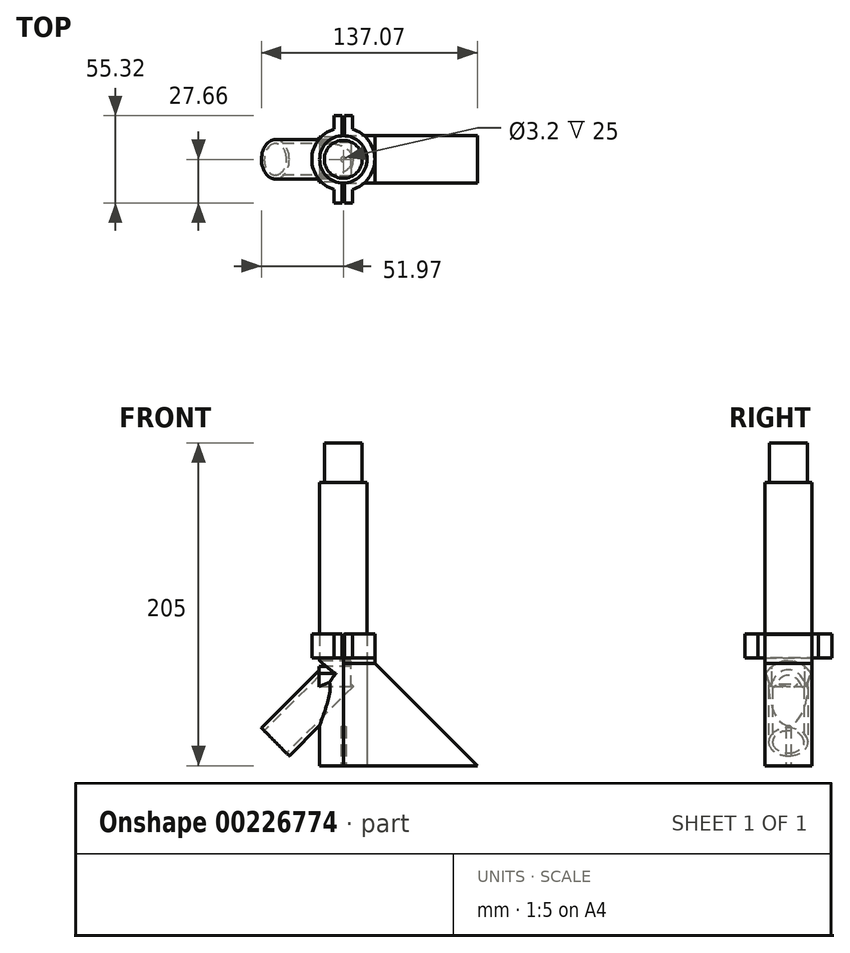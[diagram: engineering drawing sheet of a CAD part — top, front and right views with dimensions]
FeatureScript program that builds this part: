
annotation { "Feature Type Name" : "Feature", "Feature Type Description" : "" }
export const myFeature = defineFeature(function(context is Context, id is Id, definition is map)
    precondition{}
    {
        {
            var Q0;
            Q0=qCreatedBy(makeId("Top.planeOp"),FACE);
            var sketch = newSketch(context, id + "F0", { "sketchPlane" : qUnion([Q0])});
            skCircle(sketch, "E0", {"center": v(0, 0) * mm, "radius": 12 * mm});
            skCircle(sketch, "E1", {"center": v(0, 0) * mm, "radius": 15 * mm});
            skLineSegment(sketch, "E2", {"start": v(0, 15) * mm, "end": v(0, -15) * mm});
            skLineSegment(sketch, "E3", {"start": v(0, -15) * mm, "end": v(-56.85, -15) * mm});
            skLineSegment(sketch, "E4", {"start": v(-56.85, -15) * mm, "end": v(-56.85, 15) * mm});
            skLineSegment(sketch, "E5", {"start": v(-56.85, 15) * mm, "end": v(0, 15) * mm});
            skSolve(sketch);
        }
        {
            var Q0;
            {var subQ3=sQuery(id+"F0.wireOp",EDGE,"E3");Q0=makeQuery(id+"F0.imprint","IMPRINT",FACE,{"disambiguationData":[TD([[makeQuery(id+"F0.imprint","IMPRINT",EDGE,{"derivedFrom":subQ3}),-1.0]])]});}
            extrude(context, id + "F1", {"entities" : qUnion([Q0]), "depth" : 205 * mm});
        }
        {
            var Q0;
            Q0=makeQuery(id+"F0.imprint","IMPRINT",FACE,{"disambiguationData":[TD([[makeQuery(id+"F0.imprint","IMPRINT",EDGE,{"derivedFrom":sQuery(id+"F0.wireOp",EDGE,"E0")}),1.0]])]});
            var Q1;
            Q1=makeQuery(id+"F0.imprint","IMPRINT",FACE,{"disambiguationData":[TD([[makeQuery(id+"F0.imprint","IMPRINT",EDGE,{"derivedFrom":sQuery(id+"F0.wireOp",EDGE,"E0")}),-1.0]])]});
            extrude(context, id + "F2", {"entities" : qUnion([Q0, Q1]), "operationType" : NewBodyOperationType.ADD, "depth" : 10 * mm});
        }
        {
            var Q0;
            {var subQ0=sQuery(id+"F0.wireOp",EDGE,"E1");Q0=makeQuery(id+"F2.boolean.opBoolean","MERGE",FACE,{"derivedFrom":[makeQuery(id+"F1.opExtrude","CAP_FACE",FACE,{"disambiguationData":[OSD([sQuery(id+"F0.wireOp",EDGE,"E0"),subQ0])],"isStart":true}),makeQuery(id+"F2.opExtrude","CAP_FACE",FACE,{"disambiguationData":[OSD([subQ0])],"isStart":true})]});}
            var sketch = newSketch(context, id + "F3", { "sketchPlane" : qUnion([Q0])});
            skLineSegment(sketch, "E6.bottom", {"start": v(-1.5, -1.5) * mm, "end": v(1.5, -1.5) * mm});
            skLineSegment(sketch, "E6.top", {"start": v(-1.5, 1.5) * mm, "end": v(1.5, 1.5) * mm});
            skLineSegment(sketch, "E6.left", {"start": v(-1.5, -1.5) * mm, "end": v(-1.5, 1.5) * mm});
            skLineSegment(sketch, "E6.right", {"start": v(1.5, -1.5) * mm, "end": v(1.5, 1.5) * mm});
            skPoint(sketch, "E6.middle", {"position": v(0, 0) * mm});
            skCircle(sketch, "E7", {"center": v(0, 0) * mm, "radius": 2.12 * mm});
            skSolve(sketch);
        }
        {
            var Q0;
            {var subQ0=sQuery(id+"F3.wireOp",EDGE,"E6.left");Q0=makeQuery(id+"F3.imprint","IMPRINT",FACE,{"disambiguationData":[TD([[makeQuery(id+"F3.imprint","IMPRINT",EDGE,{"derivedFrom":subQ0}),1.0]])]});}
            var Q1;
            {var subQ0=sQuery(id+"F3.wireOp",EDGE,"E6.bottom");Q1=makeQuery(id+"F3.imprint","IMPRINT",FACE,{"disambiguationData":[TD([[makeQuery(id+"F3.imprint","IMPRINT",EDGE,{"derivedFrom":subQ0}),-1.0]])]});}
            var Q2;
            {var subQ0=sQuery(id+"F3.wireOp",EDGE,"E6.top");Q2=makeQuery(id+"F3.imprint","IMPRINT",FACE,{"disambiguationData":[TD([[makeQuery(id+"F3.imprint","IMPRINT",EDGE,{"derivedFrom":subQ0}),1.0]])]});}
            var Q3;
            {var subQ0=sQuery(id+"F3.wireOp",EDGE,"E6.right");Q3=makeQuery(id+"F3.imprint","IMPRINT",FACE,{"disambiguationData":[TD([[makeQuery(id+"F3.imprint","IMPRINT",EDGE,{"derivedFrom":subQ0}),-1.0]])]});}
            var Q4;
            Q4=makeQuery(id+"F3.imprint","IMPRINT",FACE,{"disambiguationData":[TD([[makeQuery(id+"F3.imprint","IMPRINT",EDGE,{"derivedFrom":sQuery(id+"F3.wireOp",EDGE,"E6.bottom")}),1.0]])]});
            extrude(context, id + "F4", {"entities" : qUnion([Q0, Q1, Q2, Q3, Q4]), "operationType" : NewBodyOperationType.REMOVE, "oppositeDirection" : true, "depth" : 18 * mm});
        }
        {
            var Q0;
            Q0=qCreatedBy(makeId("Top.planeOp"),FACE);
            var sketch = newSketch(context, id + "F5", { "sketchPlane" : qUnion([Q0])});
            skCircle(sketch, "E8", {"center": v(0, 0) * mm, "radius": 12 * mm});
            skSolve(sketch);
        }
        {
            var Q0;
            Q0=qCreatedBy(makeId("Top.planeOp"),FACE);
            var Q1;
            Q1=qCreatedBy(makeId("Right.planeOp"),FACE);
            cPlane(context, id + "F6", {"entities" : qUnion([Q0, Q1]), "cplaneType" : CPlaneType.MID_PLANE, "offset" : 25 * mm, "flipAlignment" : true, "width" : 150 * mm, "height" : 150 * mm});
        }
        {
            var Q0;
            Q0=qCreatedBy(id+"F6.planeOp",FACE);
            cPlane(context, id + "F7", {"entities" : qUnion([Q0]), "cplaneType" : CPlaneType.OFFSET, "offset" : 19.82 * mm, "oppositeDirection" : true, "width" : 150 * mm, "height" : 150 * mm});
        }
        {
            var Q0;
            Q0=qCreatedBy(id+"F7.planeOp",FACE);
            var sketch = newSketch(context, id + "F8", { "sketchPlane" : qUnion([Q0])});
            skCircle(sketch, "E9", {"center": v(0, 41.17) * mm, "radius": 10 * mm});
            skLineSegment(sketch, "E10.bottom", {"start": v(-15, 56.17) * mm, "end": v(15, 56.17) * mm});
            skLineSegment(sketch, "E10.top", {"start": v(-15, 26.17) * mm, "end": v(15, 26.17) * mm});
            skLineSegment(sketch, "E10.left", {"start": v(-15, 56.17) * mm, "end": v(-15, 26.17) * mm});
            skLineSegment(sketch, "E10.right", {"start": v(15, 56.17) * mm, "end": v(15, 26.17) * mm});
            skCircle(sketch, "E11", {"center": v(0, 41.17) * mm, "radius": 12.5 * mm});
            skSolve(sketch);
        }
        {
            var Q0;
            Q0=makeQuery(id+"F8.imprint","IMPRINT",FACE,{"disambiguationData":[TD([[makeQuery(id+"F8.imprint","IMPRINT",EDGE,{"derivedFrom":sQuery(id+"F8.wireOp",EDGE,"E9")}),-1.0]])]});
            extrude(context, id + "F9", {"entities" : qUnion([Q0]), "depth" : 59 * mm});
        }
        {
            var Q0;
            Q0=makeQuery(id+"F9.opExtrude","SWEPT_BODY",BODY,{"disambiguationData":[OSD([sQuery(id+"F8.wireOp",EDGE,"E9"),sQuery(id+"F8.wireOp",EDGE,"E11")])]});
            var Q1;
            Q1=makeQuery(id+"F1.opExtrude","SWEPT_BODY",BODY,{"disambiguationData":[OSD([sQuery(id+"F0.wireOp",EDGE,"E0"),sQuery(id+"F0.wireOp",EDGE,"E2"),sQuery(id+"F0.wireOp",EDGE,"E3"),sQuery(id+"F0.wireOp",EDGE,"E4"),sQuery(id+"F0.wireOp",EDGE,"E5")])]});
            booleanBodies(context, id + "F10", {"operationType" : BooleanOperationType.INTERSECTION, "tools" : qUnion([Q0, Q1])});
        }
        {
            var Q0;
            Q0=makeQuery(id+"F5.imprint","IMPRINT",FACE,{"disambiguationData":[TD([[makeQuery(id+"F5.imprint","IMPRINT",EDGE,{"derivedFrom":sQuery(id+"F5.wireOp",EDGE,"E8")}),1.0]])]});
            extrude(context, id + "F11", {"entities" : qUnion([Q0]), "depth" : 205 * mm});
        }
        {
            var Q0;
            Q0=makeQuery(id+"F5.imprint","IMPRINT",FACE,{"disambiguationData":[TD([[makeQuery(id+"F5.imprint","IMPRINT",EDGE,{"derivedFrom":sQuery(id+"F5.wireOp",EDGE,"E8")}),1.0]])]});
            var sketch = newSketch(context, id + "F12", { "sketchPlane" : qUnion([Q0])});
            skCircle(sketch, "E12", {"center": v(0, 0) * mm, "radius": 15 * mm});
            skSolve(sketch);
        }
        {
            var Q0;
            Q0=makeQuery(id+"F12.imprint","IMPRINT",FACE,{"disambiguationData":[TD([[makeQuery(id+"F12.imprint","IMPRINT",EDGE,{"derivedFrom":sQuery(id+"F12.wireOp",EDGE,"E12")}),1.0]])]});
            extrude(context, id + "F13", {"entities" : qUnion([Q0]), "depth" : 180 * mm});
        }
        {
            var Q0;
            Q0=makeQuery(id+"F13.opExtrude","CAP_FACE",FACE,{"disambiguationData":[OSD([sQuery(id+"F5.wireOp",EDGE,"E8"),sQuery(id+"F12.wireOp",EDGE,"E12")])],"isStart":true});
            var sketch = newSketch(context, id + "F14", { "sketchPlane" : qUnion([Q0])});
            skCircle(sketch, "E13", {"center": v(0, 0) * mm, "radius": 1.6 * mm});
            skSolve(sketch);
        }
        {
            var Q0;
            Q0=makeQuery(id+"F5.imprint","IMPRINT",FACE,{"disambiguationData":[TD([[makeQuery(id+"F5.imprint","IMPRINT",EDGE,{"derivedFrom":sQuery(id+"F5.wireOp",EDGE,"E8")}),1.0]])]});
            extrude(context, id + "F15", {"entities" : qUnion([Q0]), "operationType" : NewBodyOperationType.ADD, "depth" : 20 * mm});
        }
        {
            var Q0;
            Q0=makeQuery(id+"F14.imprint","IMPRINT",FACE,{"disambiguationData":[TD([[makeQuery(id+"F14.imprint","IMPRINT",EDGE,{"derivedFrom":sQuery(id+"F14.wireOp",EDGE,"E13")}),1.0]])]});
            extrude(context, id + "F16", {"entities" : qUnion([Q0]), "operationType" : NewBodyOperationType.REMOVE, "oppositeDirection" : true, "depth" : 25 * mm});
        }
        {
            var Q0;
            Q0=makeQuery(id+"F8.imprint","IMPRINT",FACE,{"disambiguationData":[TD([[makeQuery(id+"F8.imprint","IMPRINT",EDGE,{"derivedFrom":sQuery(id+"F8.wireOp",EDGE,"E9")}),1.0]])]});
            extrude(context, id + "F17", {"entities" : qUnion([Q0]), "operationType" : NewBodyOperationType.REMOVE, "depth" : 60 * mm});
        }
        {
            var Q0;
            Q0=qCreatedBy(id+"F7.planeOp",FACE);
            cPlane(context, id + "F18", {"entities" : qUnion([Q0]), "cplaneType" : CPlaneType.OFFSET, "offset" : 80 * mm, "width" : 150 * mm, "height" : 150 * mm});
        }
        {
            var Q0;
            {var subQ0=sQuery(id+"F5.wireOp",EDGE,"E8");Q0=makeQuery(id+"F15.boolean.opBoolean","MERGE",FACE,{"derivedFrom":[makeQuery(id+"F13.opExtrude","CAP_FACE",FACE,{"disambiguationData":[OSD([subQ0,sQuery(id+"F12.wireOp",EDGE,"E12")])],"isStart":true}),makeQuery(id+"F15.opExtrude","CAP_FACE",FACE,{"disambiguationData":[OSD([subQ0])],"isStart":true})]});}
            var sketch = newSketch(context, id + "F19", { "sketchPlane" : qUnion([Q0])});
            skLineSegment(sketch, "E14.bottom", {"start": v(-15, -15) * mm, "end": v(85.1, -15) * mm});
            skLineSegment(sketch, "E14.top", {"start": v(-15, 15) * mm, "end": v(85.1, 15) * mm});
            skLineSegment(sketch, "E14.left", {"start": v(-15, -15) * mm, "end": v(-15, 15) * mm});
            skLineSegment(sketch, "E14.right", {"start": v(85.1, -15) * mm, "end": v(85.1, 15) * mm});
            skSolve(sketch);
        }
        {
            var Q0;
            {var subQ0=sQuery(id+"F19.wireOp",EDGE,"E14.right");Q0=makeQuery(id+"F19.imprint","IMPRINT",FACE,{"disambiguationData":[TD([[makeQuery(id+"F19.imprint","IMPRINT",EDGE,{"derivedFrom":subQ0}),1.0]])]});}
            extrude(context, id + "F20", {"entities" : qUnion([Q0]), "oppositeDirection" : true, "depth" : 65 * mm});
        }
        {
            var Q0;
            Q0=qCreatedBy(makeId("Right.planeOp"),FACE);
            cPlane(context, id + "F21", {"entities" : qUnion([Q0]), "cplaneType" : CPlaneType.OFFSET, "offset" : 15 * mm, "oppositeDirection" : true, "width" : 150 * mm, "height" : 150 * mm});
        }
        {
            var Q0;
            Q0=qCreatedBy(id+"F21.planeOp",FACE);
            var sketch = newSketch(context, id + "F22", { "sketchPlane" : qUnion([Q0])});
            skCircle(sketch, "E15", {"center": v(0, 50) * mm, "radius": 18.58 * mm});
            skCircle(sketch, "E16", {"center": v(0, 50) * mm, "radius": 16.65 * mm});
            skLineSegment(sketch, "E17", {"start": v(18.58, 50) * mm, "end": v(-18.58, 50) * mm});
            skLineSegment(sketch, "E18", {"start": v(-10.5, 50) * mm, "end": v(-10.5, 37.08) * mm});
            skLineSegment(sketch, "E19", {"start": v(0, 0) * mm, "end": v(0, 91.56) * mm, "construction": true});
            skLineSegment(sketch, "E20", {"start": v(-11.29, 50) * mm, "end": v(-14.29, 41.45) * mm});
            skLineSegment(sketch, "E21.MirrorCS", {"start": v(10.5, 50) * mm, "end": v(10.5, 37.08) * mm});
            skLineSegment(sketch, "E22.MirrorCS", {"start": v(11.29, 50) * mm, "end": v(14.29, 41.45) * mm});
            skLineSegment(sketch, "E23.MirrorCS", {"start": v(-10.5, 50) * mm, "end": v(-10.5, 62.92) * mm});
            skLineSegment(sketch, "E24.MirrorCS", {"start": v(-11.29, 50) * mm, "end": v(-14.29, 58.55) * mm});
            skLineSegment(sketch, "E25.MirrorCS", {"start": v(10.5, 50) * mm, "end": v(10.5, 62.92) * mm});
            skLineSegment(sketch, "E26.MirrorCS", {"start": v(11.29, 50) * mm, "end": v(14.29, 58.55) * mm});
            skPoint(sketch, "E27", {"position": v(0, 68.58) * mm});
            skSolve(sketch);
        }
        {
            var Q0;
            {var subQ0=sQuery(id+"F22.wireOp",EDGE,"E23.MirrorCS");Q0=makeQuery(id+"F22.imprint","IMPRINT",FACE,{"disambiguationData":[TD([[makeQuery(id+"F22.imprint","IMPRINT",EDGE,{"derivedFrom":subQ0}),-1.0]])]});}
            extrude(context, id + "F23", {"entities" : qUnion([Q0]), "operationType" : NewBodyOperationType.REMOVE, "depth" : 20 * mm});
        }
        {
            var Q0;
            {var subQ0=sQuery(id+"F22.wireOp",EDGE,"E23.MirrorCS");Q0=makeQuery(id+"F22.imprint","IMPRINT",FACE,{"disambiguationData":[TD([[makeQuery(id+"F22.imprint","IMPRINT",EDGE,{"derivedFrom":subQ0}),1.0]])]});}
            var Q1;
            {var subQ0=sQuery(id+"F22.wireOp",EDGE,"E25.MirrorCS");Q1=makeQuery(id+"F22.imprint","IMPRINT",FACE,{"disambiguationData":[TD([[makeQuery(id+"F22.imprint","IMPRINT",EDGE,{"derivedFrom":subQ0}),-1.0]])]});}
            extrude(context, id + "F24", {"entities" : qUnion([Q0, Q1]), "operationType" : NewBodyOperationType.ADD, "depth" : 18 * mm});
        }
        {
            var Q0;
            {var subQ0=sQuery(id+"F22.wireOp",EDGE,"E23.MirrorCS");Q0=makeQuery(id+"F22.imprint","IMPRINT",FACE,{"disambiguationData":[TD([[makeQuery(id+"F22.imprint","IMPRINT",EDGE,{"derivedFrom":subQ0}),1.0]])]});}
            var Q1;
            {var subQ0=sQuery(id+"F22.wireOp",EDGE,"E25.MirrorCS");Q1=makeQuery(id+"F22.imprint","IMPRINT",FACE,{"disambiguationData":[TD([[makeQuery(id+"F22.imprint","IMPRINT",EDGE,{"derivedFrom":subQ0}),-1.0]])]});}
            extrude(context, id + "F25", {"entities" : qUnion([Q0, Q1]), "operationType" : NewBodyOperationType.ADD, "oppositeDirection" : true, "depth" : .5 * mm});
        }
        {
            var Q0;
            Q0=qCreatedBy(makeId("Top.planeOp"),FACE);
            cPlane(context, id + "F26", {"entities" : qUnion([Q0]), "cplaneType" : CPlaneType.OFFSET, "offset" : 68.58 * mm, "width" : 150 * mm, "height" : 150 * mm});
        }
        {
            var Q0;
            Q0=qCreatedBy(id+"F26.planeOp",FACE);
            var sketch = newSketch(context, id + "F27", { "sketchPlane" : qUnion([Q0])});
            skCircle(sketch, "E28", {"center": v(0, 0) * mm, "radius": 15 * mm});
            skCircle(sketch, "E29", {"center": v(0, 0) * mm, "radius": 20 * mm});
            skLineSegment(sketch, "E30", {"start": v(0.75, -19.99) * mm, "end": v(0.75, -14.98) * mm});
            skLineSegment(sketch, "E31.MirrorCS", {"start": v(-0.75, -19.99) * mm, "end": v(-0.75, -14.98) * mm});
            skLineSegment(sketch, "E32.trimOffspring", {"start": v(-0.75, 14.98) * mm, "end": v(-0.75, 19.99) * mm});
            skLineSegment(sketch, "E33.trimOffspring", {"start": v(0.75, 14.98) * mm, "end": v(0.75, 19.99) * mm});
            skLineSegment(sketch, "E34", {"start": v(-0.75, -19.99) * mm, "end": v(-0.75, -27.66) * mm});
            skLineSegment(sketch, "E35", {"start": v(-0.75, -27.66) * mm, "end": v(-5.75, -27.66) * mm});
            skLineSegment(sketch, "E36", {"start": v(-5.75, -27.66) * mm, "end": v(-5.75, -19.16) * mm});
            skLineSegment(sketch, "E37", {"start": v(0.75, -19.99) * mm, "end": v(0.75, -27.66) * mm});
            skLineSegment(sketch, "E38", {"start": v(0.75, -27.66) * mm, "end": v(5.75, -27.66) * mm});
            skLineSegment(sketch, "E39", {"start": v(5.75, -27.66) * mm, "end": v(5.75, -19.16) * mm});
            skLineSegment(sketch, "E40", {"start": v(-5.75, 19.16) * mm, "end": v(-5.75, 27.66) * mm});
            skLineSegment(sketch, "E41", {"start": v(-5.75, 27.66) * mm, "end": v(-0.75, 27.66) * mm});
            skLineSegment(sketch, "E42", {"start": v(-0.75, 27.66) * mm, "end": v(-0.75, 19.99) * mm});
            skLineSegment(sketch, "E43", {"start": v(0.75, 19.99) * mm, "end": v(0.75, 27.66) * mm});
            skLineSegment(sketch, "E44", {"start": v(0.75, 27.66) * mm, "end": v(5.75, 27.66) * mm});
            skLineSegment(sketch, "E45", {"start": v(5.75, 27.66) * mm, "end": v(5.75, 19.16) * mm});
            skLineSegment(sketch, "E46", {"start": v(0, -20) * mm, "end": v(0, 20) * mm, "construction": true});
            skSolve(sketch);
        }
        {
            var Q0;
            {var subQ0=sQuery(id+"F27.wireOp",EDGE,"E31.MirrorCS");Q0=makeQuery(id+"F27.imprint","IMPRINT",FACE,{"disambiguationData":[TD([[makeQuery(id+"F27.imprint","IMPRINT",EDGE,{"derivedFrom":subQ0}),1.0]])]});}
            var Q1;
            {var subQ0=sQuery(id+"F27.wireOp",EDGE,"E34");Q1=makeQuery(id+"F27.imprint","IMPRINT",FACE,{"disambiguationData":[TD([[makeQuery(id+"F27.imprint","IMPRINT",EDGE,{"derivedFrom":subQ0}),-1.0]])]});}
            var Q2;
            {var subQ0=sQuery(id+"F27.wireOp",EDGE,"E37");Q2=makeQuery(id+"F27.imprint","IMPRINT",FACE,{"disambiguationData":[TD([[makeQuery(id+"F27.imprint","IMPRINT",EDGE,{"derivedFrom":subQ0}),1.0]])]});}
            var Q3;
            {var subQ3=sQuery(id+"F27.wireOp",EDGE,"E30");Q3=makeQuery(id+"F27.imprint","IMPRINT",FACE,{"disambiguationData":[TD([[makeQuery(id+"F27.imprint","IMPRINT",EDGE,{"derivedFrom":subQ3}),-1.0]])]});}
            var Q4;
            {var subQ0=sQuery(id+"F27.wireOp",EDGE,"E43");Q4=makeQuery(id+"F27.imprint","IMPRINT",FACE,{"disambiguationData":[TD([[makeQuery(id+"F27.imprint","IMPRINT",EDGE,{"derivedFrom":subQ0}),-1.0]])]});}
            var Q5;
            {var subQ2=sQuery(id+"F27.wireOp",EDGE,"E40");Q5=makeQuery(id+"F27.imprint","IMPRINT",FACE,{"disambiguationData":[TD([[makeQuery(id+"F27.imprint","IMPRINT",EDGE,{"derivedFrom":subQ2}),-1.0]])]});}
            extrude(context, id + "F28", {"entities" : qUnion([Q0, Q1, Q2, Q3, Q4, Q5]), "depth" : 15 * mm});
        }
        {
            var Q0;
            Q0=makeQuery(id+"F20.opExtrude","CAP_EDGE",EDGE,{"disambiguationData":[OSD([sQuery(id+"F19.wireOp",EDGE,"E14.right")])],"isStart":false});
            chamfer(context, id + "F29", {"entities" : qUnion([Q0]), "width" : 65 * mm, "tangentPropagation" : true});
        }
        {
            var Q0;
            Q0=makeQuery(id+"F20.opExtrude","CAP_FACE",FACE,{"disambiguationData":[OSD([sQuery(id+"F12.wireOp",EDGE,"E12"),sQuery(id+"F19.wireOp",EDGE,"E14.bottom"),sQuery(id+"F19.wireOp",EDGE,"E14.top"),sQuery(id+"F19.wireOp",EDGE,"E14.right")])],"isStart":false});
            extrude(context, id + "F30", {"entities" : qUnion([Q0]), "depth" : 18.5 * mm});
        }
    });
